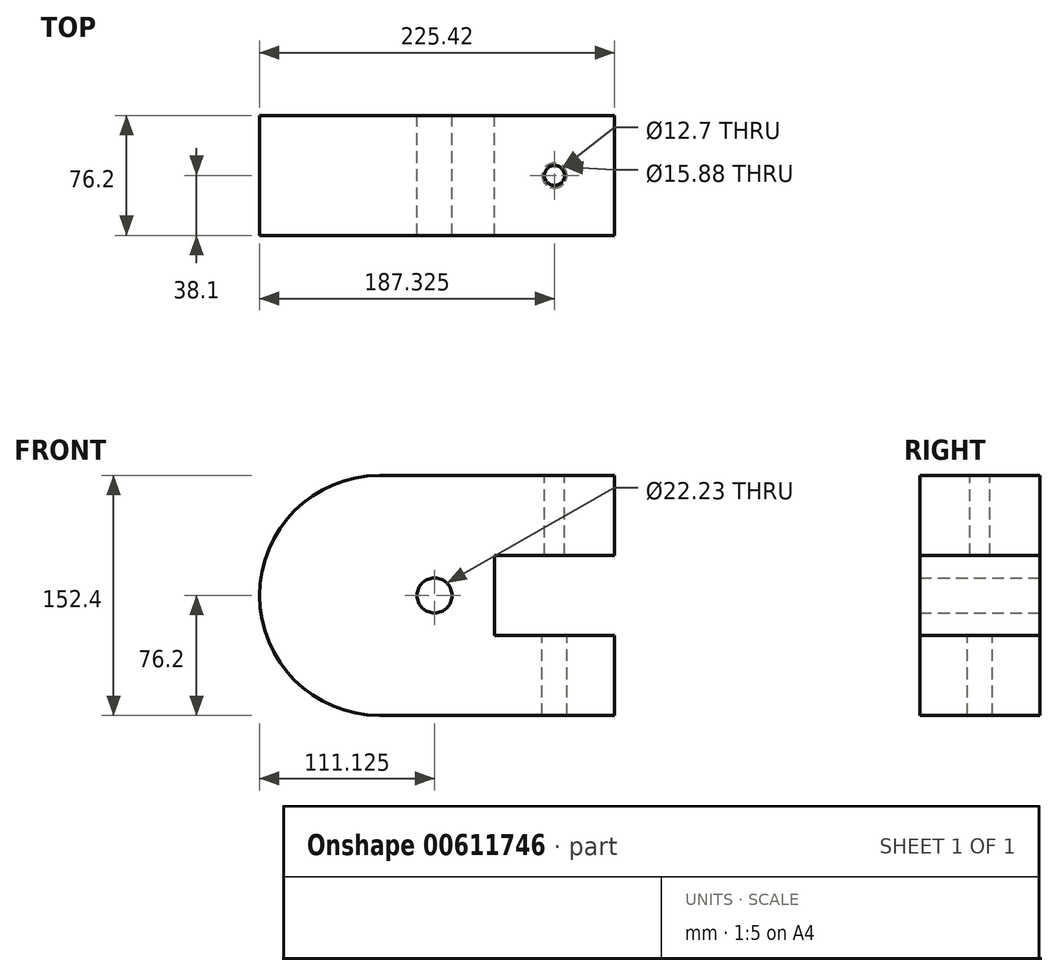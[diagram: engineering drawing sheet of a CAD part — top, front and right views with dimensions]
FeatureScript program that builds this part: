
annotation { "Feature Type Name" : "Feature", "Feature Type Description" : "" }
export const myFeature = defineFeature(function(context is Context, id is Id, definition is map)
    precondition{}
    {
        {
            var Q0;
            Q0=qCreatedBy(makeId("Front.planeOp"),FACE);
            var sketch = newSketch(context, id + "F0", { "sketchPlane" : qUnion([Q0])});
            skLineSegment(sketch, "E0", {"start": v(0, 76.2) * mm, "end": v(0, 76.2) * mm});
            skLineSegment(sketch, "E1", {"start": v(76.2, 152.4) * mm, "end": v(225.43, 152.4) * mm});
            skLineSegment(sketch, "E2", {"start": v(225.43, 152.4) * mm, "end": v(225.43, 101.6) * mm});
            skLineSegment(sketch, "E3", {"start": v(225.43, 101.6) * mm, "end": v(149.22, 101.6) * mm});
            skLineSegment(sketch, "E4", {"start": v(149.22, 101.6) * mm, "end": v(149.22, 50.8) * mm});
            skLineSegment(sketch, "E5", {"start": v(149.22, 50.8) * mm, "end": v(225.43, 50.8) * mm});
            skLineSegment(sketch, "E6", {"start": v(225.43, 50.8) * mm, "end": v(225.43, 0) * mm});
            skLineSegment(sketch, "E7", {"start": v(225.43, 0) * mm, "end": v(76.2, 0) * mm});
            skCircle(sketch, "E8", {"center": v(111.12, 76.2) * mm, "radius": 11.11 * mm});
            skPoint(sketch, "E9", {"position": v(0, 76.2) * mm});
            skPoint(sketch, "E10.visualSharp", {"position": v(0, 152.4) * mm});
            skArc(sketch, "E10.filletArc", {"start": v(76.2, 152.4) * mm, "mid": v(22.32, 130.08) * mm, "end": v(0, 76.2) * mm});
            skPoint(sketch, "E11.visualSharp", {"position": v(0, 0) * mm});
            skArc(sketch, "E11.filletArc", {"start": v(0, 76.2) * mm, "mid": v(22.32, 22.32) * mm, "end": v(76.2, 0) * mm});
            skSolve(sketch);
        }
        {
            var Q0;
            Q0=makeQuery(id+"F0.imprint","IMPRINT",FACE,{"disambiguationData":[TD([[makeQuery(id+"F0.imprint","IMPRINT",EDGE,{"derivedFrom":sQuery(id+"F0.wireOp",EDGE,"E1")}),-1.0]])]});
            extrude(context, id + "F1", {"entities" : qUnion([Q0]), "depth" : 76.2 * mm, "offsetDistance" : 25.4 * mm});
        }
        {
            var Q0;
            Q0=makeQuery(id+"F1.opExtrude","SWEPT_FACE",FACE,{"disambiguationData":[OSD([sQuery(id+"F0.wireOp",EDGE,"E1")])]});
            var sketch = newSketch(context, id + "F2", { "sketchPlane" : qUnion([Q0])});
            skCircle(sketch, "E12", {"center": v(187.33, -38.1) * mm, "radius": 6.35 * mm});
            skSolve(sketch);
        }
        {
            var Q0;
            Q0=makeQuery(id+"F2.imprint","IMPRINT",FACE,{"disambiguationData":[TD([[makeQuery(id+"F2.imprint","IMPRINT",EDGE,{"derivedFrom":sQuery(id+"F2.wireOp",EDGE,"E12")}),1.0]])]});
            extrude(context, id + "F3", {"entities" : qUnion([Q0]), "operationType" : NewBodyOperationType.REMOVE, "oppositeDirection" : true, "depth" : 81.03 * mm, "offsetDistance" : 25.4 * mm});
        }
        {
            var Q0;
            Q0=makeQuery(id+"F1.opExtrude","SWEPT_FACE",FACE,{"disambiguationData":[OSD([sQuery(id+"F0.wireOp",EDGE,"E5")])]});
            var sketch = newSketch(context, id + "F4", { "sketchPlane" : qUnion([Q0])});
            skCircle(sketch, "E13", {"center": v(187.33, -38.1) * mm, "radius": 7.94 * mm});
            skSolve(sketch);
        }
        {
            var Q0;
            Q0=makeQuery(id+"F4.imprint","IMPRINT",FACE,{"disambiguationData":[TD([[makeQuery(id+"F4.imprint","IMPRINT",EDGE,{"derivedFrom":sQuery(id+"F4.wireOp",EDGE,"E13")}),1.0]])]});
            extrude(context, id + "F5", {"entities" : qUnion([Q0]), "operationType" : NewBodyOperationType.REMOVE, "oppositeDirection" : true, "depth" : 65.28 * mm, "offsetDistance" : 25.4 * mm});
        }
    });
